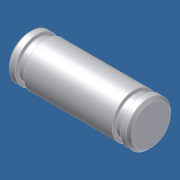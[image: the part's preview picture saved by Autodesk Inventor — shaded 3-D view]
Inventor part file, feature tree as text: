
AUTODESK INVENTOR PART (.ipt)
format: ipt  version: 2012 (Build 160160000, 160)  size: 124,928 bytes
history: native  units: in
note: dims shown in document units (in); Inventor stores cm internally (conversion verified against a paired STEP export)
features: other x49, revolve x1, sketch x1
ambient origin geometry x8: Origin, YZ Plane, XZ Plane, XY Plane, X Axis, Y Axis, Z Axis, Center Point
bodies: Solid1 (feature_tree)
feature tree (51):
  revolve  "Revolution1"  [1 undecoded]
  other  "pin_XY"
  other  "pin_YZ"
  other  "pin_ZX"
  other  "pin_X"
  other  "pin_Y"
  other  "pin_Z"
  other  "pin_Center"
  other  "rr1_XY"
  other  "rr1_YZ"
  other  "rr1_ZX"
  other  "rr1_X"
  other  "rr1_Y"
  other  "rr1_Z"
  other  "rr1_Center"
  other  "rr2_XY"
  other  "rr2_YZ"
  other  "rr2_ZX"
  other  "rr2_X"
  other  "rr2_Y"
  other  "rr2_Z"
  other  "rr2_Center"
  other  "w21_XY"
  other  "w21_YZ"
  other  "w21_ZX"
  other  "w21_X"
  other  "w21_Y"
  other  "w21_Z"
  other  "w21_Center"
  other  "w22_XY"
  other  "w22_YZ"
  other  "w22_ZX"
  other  "w22_X"
  other  "w22_Y"
  other  "w22_Z"
  other  "w22_Center"
  other  "p1_XY"
  other  "p1_YZ"
  other  "p1_ZX"
  other  "p1_X"
  other  "p1_Y"
  other  "p1_Z"
  other  "p1_Center"
  other  "p2_XY"
  other  "p2_YZ"
  other  "p2_ZX"
  other  "p2_X"
  other  "p2_Y"
  other  "p2_Z"
  other  "p2_Center"
  sketch  "Sketch_1"  dims[d0=360.0deg]
note: 1 required parameter value undecoded (feature->parameter linkage not recoverable at this tier; creation-order binding heuristic only, values carry confidence <= 0.55)
